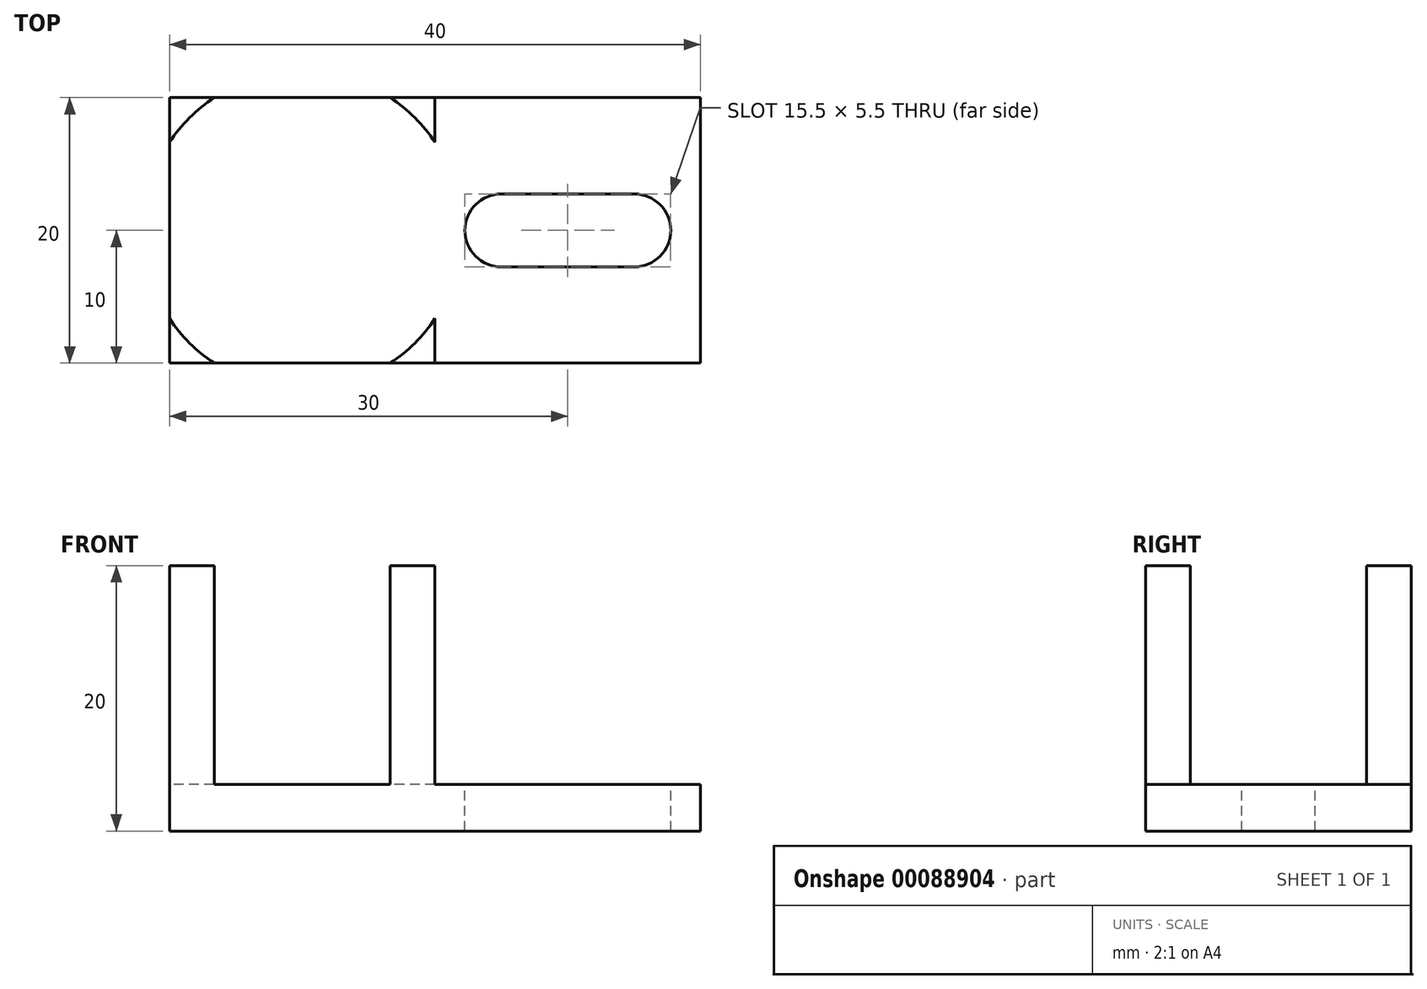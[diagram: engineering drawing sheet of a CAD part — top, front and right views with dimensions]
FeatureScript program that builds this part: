
annotation { "Feature Type Name" : "Feature", "Feature Type Description" : "" }
export const myFeature = defineFeature(function(context is Context, id is Id, definition is map)
    precondition{}
    {
        {
            var Q0;
            Q0=qCreatedBy(makeId("Front.planeOp"),FACE);
            var sketch = newSketch(context, id + "F0", { "sketchPlane" : qUnion([Q0])});
            skLineSegment(sketch, "E0.bottom", {"start": v(0, 0) * mm, "end": v(20, 0) * mm});
            skLineSegment(sketch, "E0.top", {"start": v(0, 20) * mm, "end": v(20, 20) * mm});
            skLineSegment(sketch, "E0.left", {"start": v(0, 0) * mm, "end": v(0, 20) * mm});
            skLineSegment(sketch, "E0.right", {"start": v(20, 3.5) * mm, "end": v(20, 20) * mm});
            skLineSegment(sketch, "E1.bottom", {"start": v(20, 0) * mm, "end": v(40, 0) * mm});
            skLineSegment(sketch, "E1.top", {"start": v(20, 3.5) * mm, "end": v(40, 3.5) * mm});
            skLineSegment(sketch, "E1.right", {"start": v(40, 0) * mm, "end": v(40, 3.5) * mm});
            skSolve(sketch);
        }
        {
            var Q0;
            Q0=makeQuery(id+"F0.imprint","IMPRINT",FACE,{"disambiguationData":[TD([[makeQuery(id+"F0.imprint","IMPRINT",EDGE,{"derivedFrom":sQuery(id+"F0.wireOp",EDGE,"E0.bottom")}),1.0]])]});
            extrude(context, id + "F1", {"entities" : qUnion([Q0]), "depth" : 20 * mm});
        }
        {
            var Q0;
            Q0=makeQuery(id+"F1.opExtrude","SWEPT_FACE",FACE,{"disambiguationData":[OSD([sQuery(id+"F0.wireOp",EDGE,"E0.top")])]});
            var sketch = newSketch(context, id + "F2", { "sketchPlane" : qUnion([Q0])});
            skCircle(sketch, "E2", {"center": v(10, -10) * mm, "radius": 12 * mm});
            skLineSegment(sketch, "E3", {"start": v(0, 0) * mm, "end": v(20, -20) * mm, "construction": true});
            skLineSegment(sketch, "E4", {"start": v(0, -20) * mm, "end": v(20, 0) * mm, "construction": true});
            skSolve(sketch);
        }
        {
            var Q0;
            Q0 = qSketchRegion(id + "F2", true);
            var Q1;
            Q1=makeQuery(id+"F1.opExtrude","SWEPT_FACE",FACE,{"disambiguationData":[OSD([sQuery(id+"F0.wireOp",EDGE,"E1.top")])]});
            extrude(context, id + "F3", {"entities" : qUnion([Q0]), "operationType" : NewBodyOperationType.REMOVE, "endBound" : BoundingType.UP_TO_SURFACE, "oppositeDirection" : true, "endBoundEntityFace" : qUnion([Q1]), "depth" : 25 * mm});
        }
        {
            var Q0;
            {var subQ0=sQuery(id+"F0.wireOp",EDGE,"E1.top");Q0=makeQuery(id+"F3.boolean.opBoolean","MERGE",FACE,{"derivedFrom":[makeQuery(id+"F1.opExtrude","SWEPT_FACE",FACE,{"disambiguationData":[OSD([subQ0])]}),makeQuery(id+"F3.opExtrude","CAP_FACE",FACE,{"disambiguationData":[OSD([subQ0])],"isStart":false})]});}
            var sketch = newSketch(context, id + "F4", { "sketchPlane" : qUnion([Q0])});
            skLineSegment(sketch, "E5", {"start": v(59.51, -10) * mm, "end": v(-6.72, -10) * mm, "construction": true});
            skArc(sketch, "E6", {"start": v(35, -12.75) * mm, "mid": v(37.75, -10) * mm, "end": v(35, -7.25) * mm});
            skLineSegment(sketch, "E7", {"start": v(30, 22.42) * mm, "end": v(30, -54.54) * mm, "construction": true});
            skLineSegment(sketch, "E8", {"start": v(35, -7.25) * mm, "end": v(30, -7.25) * mm});
            skLineSegment(sketch, "E9", {"start": v(35, -12.75) * mm, "end": v(30, -12.75) * mm});
            skLineSegment(sketch, "E10.MirrorCS", {"start": v(25, -12.75) * mm, "end": v(30, -12.75) * mm});
            skArc(sketch, "E11.MirrorCS", {"start": v(25, -12.75) * mm, "mid": v(22.25, -10) * mm, "end": v(25, -7.25) * mm});
            skLineSegment(sketch, "E12.MirrorCS", {"start": v(25, -7.25) * mm, "end": v(30, -7.25) * mm});
            skSolve(sketch);
        }
        {
            var Q0;
            Q0 = qSketchRegion(id + "F4", true);
            extrude(context, id + "F5", {"entities" : qUnion([Q0]), "operationType" : NewBodyOperationType.REMOVE, "endBound" : BoundingType.UP_TO_NEXT, "oppositeDirection" : true, "depth" : 25 * mm});
        }
    });
